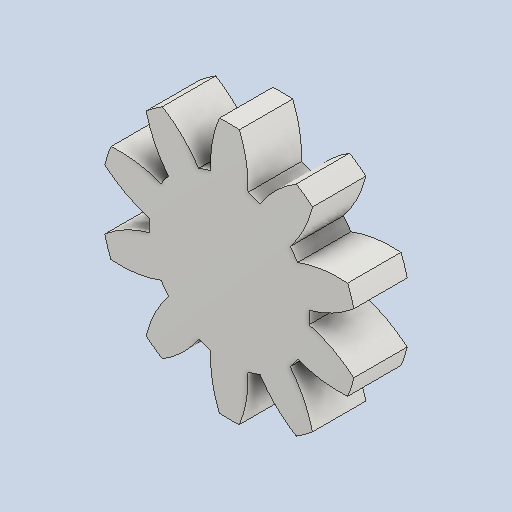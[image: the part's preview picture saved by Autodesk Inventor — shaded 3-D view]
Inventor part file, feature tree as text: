
AUTODESK INVENTOR PART (.ipt)
format: ipt  version: 2023 (Build 270158000, 158)  size: 193,536 bytes
history: native  units: mm (DEFAULTED — no unit token found)
features: plane x3, other x3, sketch x2, extrude x1
ambient origin geometry x8: Origin, YZ Plane, XZ Plane, XY Plane, X Axis, Y Axis, Z Axis, Center Point
bodies: Solid1 (feature_tree)
feature tree (9):
  extrude  "Extrusion1"  Depth=5.0mm TaperAngle=0.0deg
  plane  "Work Plane2"
  plane  "Work Plane8"
  plane  "Work Plane9"
  other  "Spur Gear"
  sketch  "Sketch1"  dims[d0=24.0mm d1=5.0mm d2=0.0mm]
  sketch  "Sketch2"  dims[d3=20.0mm d4=10.0mm d5=0.0mm d16=40.0mm d17=0.0mm d34=3.141593mm d39=0.0mm d41=0.0mm d43=40.0mm d46=40.0mm d47=0.0mm d48=0.0mm]
  other  "Srf1"
  other  "Pitch Diameter"
